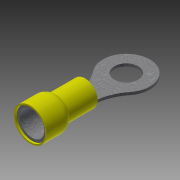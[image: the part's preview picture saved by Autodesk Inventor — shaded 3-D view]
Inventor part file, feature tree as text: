
AUTODESK INVENTOR PART (.ipt)
format: ipt  version: 2014 (Build 180170000, 170)  size: 418,304 bytes
history: native  units: in
note: dims shown in document units (in); Inventor stores cm internally (conversion verified against a paired STEP export)
features: sketch x7, fillet x5, projected_geometry x5, extrude x4, shell x1, revolve x1, plane x1, loft x1, chamfer x1, other x1
ambient origin geometry x8: Origin, YZ Plane, XZ Plane, XY Plane, X Axis, Y Axis, Z Axis, Center Point
bodies: Solid1 (feature_tree), Solid2 (feature_tree)
feature tree (27):
  extrude  "Extrusion1"  Depth=0.336in TaperAngle=0.0deg
  extrude  "Extrusion2"  Depth=0.28in TaperAngle=0.0deg
  fillet  "Fillet1"  Radius=0.02in
  fillet  "Fillet2"  Radius=0.1in
  shell  "Shell1"  Thickness=0.0165in
  revolve  "Revolution1"  [1 undecoded]
  sketch  "Sketch4"  dims[d12=0.529in d13=0.1315in]
  plane  "Work Plane1"
  extrude  "Extrusion3"  Depth=0.1315in
  loft  "Loft1"
  fillet  "Fillet3"  [1 undecoded]
  fillet  "Fillet4"  [1 undecoded]
  fillet  "Fillet5"  Radius=0.02in
  extrude  "Extrusion4"  Depth=0.01in
  chamfer  "Chamfer1"  Distance=0.005in
  sketch  "Sketch1"  dims[d0=0.285in d1=0.336in d2=0.0in]
  sketch  "Sketch2"  dims[d3=0.372in d4=0.28in d5=0.0in d6=0.02in d7=0.1in d8=0.0165in]
  projected_geometry  "Projected Loop1"
  sketch  "Sketch3"  dims[d10=90.0deg d11=0.466in]
  sketch  "Sketch5"  dims[d14=-0.0685in d15=0.03in d16=0.0in d17=0.0in d18=90.0deg d19=0.0in d20=90.0deg d21=0.02in]
  sketch  "Sketch6"  dims[d22=0.02in d23=0.01in]
  projected_geometry  "Projected Loop2"
  other  "Edges1"
  sketch  "Sketch7"  dims[d24=0.03in d25=0.005in d26=0.0395in d27=0.0in d28=0.002in d29=0.125in d30=45.0deg]
  projected_geometry  "Projected Loop3"
  projected_geometry  "Project Cut Edges1"
  projected_geometry  "Project Cut Edges2"
note: 3 required parameter values undecoded (feature->parameter linkage not recoverable at this tier; creation-order binding heuristic only, values carry confidence <= 0.55)